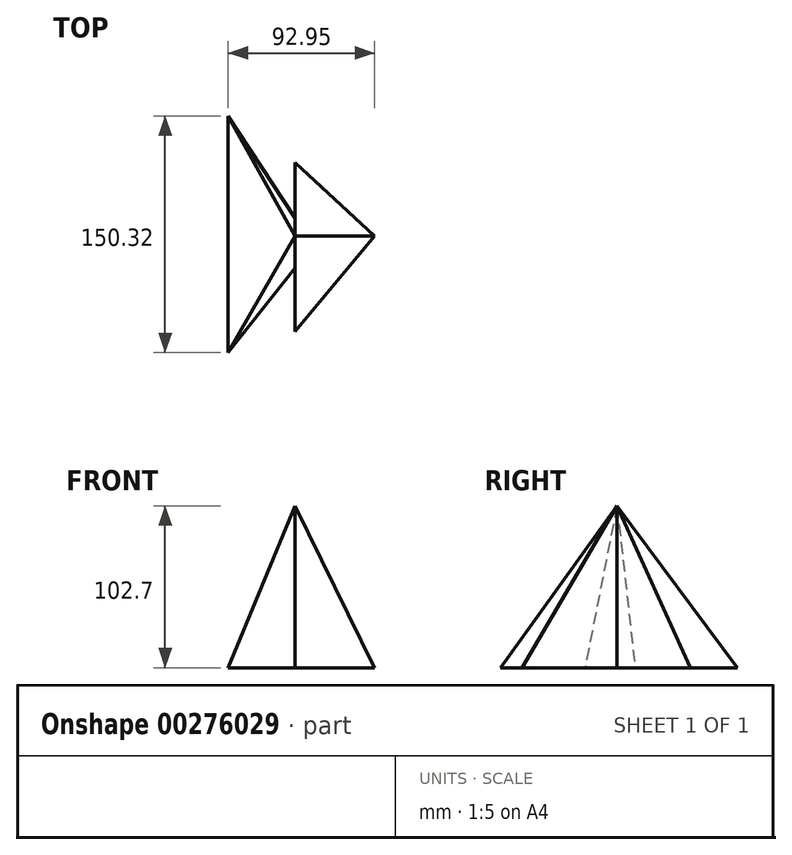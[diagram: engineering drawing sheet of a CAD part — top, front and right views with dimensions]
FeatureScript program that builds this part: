
annotation { "Feature Type Name" : "Feature", "Feature Type Description" : "" }
export const myFeature = defineFeature(function(context is Context, id is Id, definition is map)
    precondition{}
    {
        {
            var Q0;
            Q0=qCreatedBy(makeId("Top.planeOp"),FACE);
            var sketch = newSketch(context, id + "F0", { "sketchPlane" : qUnion([Q0])});
            skLineSegment(sketch, "E0", {"start": v(-42.46, 76.45) * mm, "end": v(-42.46, -73.87) * mm});
            skLineSegment(sketch, "E1", {"start": v(-42.46, -73.87) * mm, "end": v(0, -20.23) * mm});
            skLineSegment(sketch, "E2", {"start": v(0, -60.39) * mm, "end": v(0, -20.23) * mm});
            skLineSegment(sketch, "E3", {"start": v(0, -60.39) * mm, "end": v(50.5, 0) * mm});
            skLineSegment(sketch, "E4", {"start": v(50.5, 0) * mm, "end": v(0, 46.62) * mm});
            skLineSegment(sketch, "E5", {"start": v(0, 46.62) * mm, "end": v(0, 10.76) * mm});
            skLineSegment(sketch, "E6", {"start": v(0.57, 10.76) * mm, "end": v(-42.46, 76.45) * mm});
            skSolve(sketch);
        }
        {
            var Q0;
            Q0=qCreatedBy(makeId("Top.planeOp"),FACE);
            cPlane(context, id + "F1", {"entities" : qUnion([Q0]), "cplaneType" : CPlaneType.OFFSET, "offset" : 102.7 * mm, "width" : 150 * mm, "height" : 150 * mm});
        }
        {
            var Q0;
            Q0=qCreatedBy(id+"F1.planeOp",FACE);
            var sketch = newSketch(context, id + "F2", { "sketchPlane" : qUnion([Q0])});
            skPoint(sketch, "E7", {"position": v(0, 0) * mm});
            skSolve(sketch);
        }
        {
            var Q0;
            Q0=sQuery(id+"F2.wireOp",VERTEX,"E7");
            var Q1;
            {var subQ0=sQuery(id+"F0.wireOp",EDGE,"E0");Q1=makeQuery(id+"F0.imprint","IMPRINT",FACE,{"disambiguationData":[TD([[makeQuery(id+"F0.imprint","IMPRINT",EDGE,{"derivedFrom":subQ0}),1.0]])]});}
            loft(context, id + "F3", {"sheetProfilesArray" : [{ "sheetProfileEntities" : qUnion([Q0]) }, { "sheetProfileEntities" : qUnion([Q1]) }]});
        }
    });
